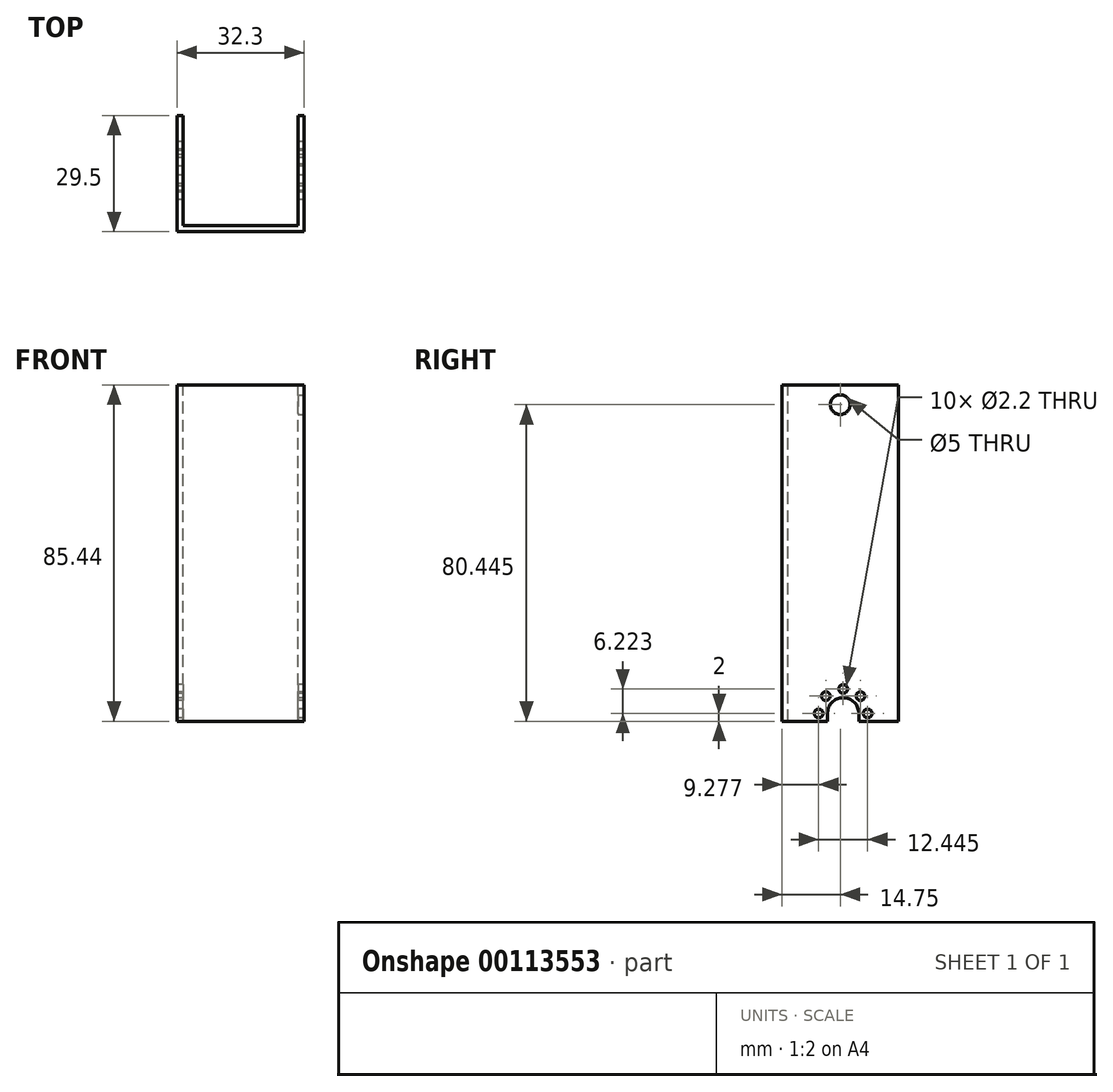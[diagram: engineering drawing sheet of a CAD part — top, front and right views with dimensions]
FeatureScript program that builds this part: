
annotation { "Feature Type Name" : "Feature", "Feature Type Description" : "" }
export const myFeature = defineFeature(function(context is Context, id is Id, definition is map)
    precondition{}
    {
        {
            var Q0;
            Q0=qCreatedBy(makeId("Front.planeOp"),FACE);
            var sketch = newSketch(context, id + "F0", { "sketchPlane" : qUnion([Q0])});
            skLineSegment(sketch, "E0.bottom", {"start": v(0, 0) * mm, "end": v(1.5, 0) * mm});
            skLineSegment(sketch, "E0.top", {"start": v(0, 86.95) * mm, "end": v(32.3, 86.95) * mm});
            skLineSegment(sketch, "E0.left", {"start": v(0, 0) * mm, "end": v(0, 86.95) * mm});
            skLineSegment(sketch, "E0.right", {"start": v(32.3, 0) * mm, "end": v(32.3, 86.95) * mm});
            skLineSegment(sketch, "E1.top", {"start": v(1.5, 85.45) * mm, "end": v(30.8, 85.45) * mm});
            skLineSegment(sketch, "E1.left", {"start": v(1.5, 0) * mm, "end": v(1.5, 85.45) * mm});
            skLineSegment(sketch, "E1.right", {"start": v(30.8, 0) * mm, "end": v(30.8, 85.45) * mm});
            skLineSegment(sketch, "E2.trimOffspring", {"start": v(30.8, 0) * mm, "end": v(32.3, 0) * mm});
            skSolve(sketch);
        }
        {
            var Q0;
            Q0=qSketchRegion(id+"F0",true);
            extrude(context, id + "F1", {"entities" : qUnion([Q0]), "depth" : 28 * mm});
        }
        {
            var Q0;
            Q0=makeQuery(id+"F1.opExtrude","SWEPT_FACE",FACE,{"disambiguationData":[OSD([sQuery(id+"F0.wireOp",EDGE,"E0.left")])]});
            var sketch = newSketch(context, id + "F2", { "sketchPlane" : qUnion([Q0])});
            skArc(sketch, "E3", {"start": v(18, 2) * mm, "mid": v(14, 6) * mm, "end": v(10, 2) * mm});
            skCircle(sketch, "E4", {"center": v(20.22, 2) * mm, "radius": 1.1 * mm});
            skCircle(sketch, "E5.1.0", {"center": v(18.4, 6.4) * mm, "radius": 1.1 * mm});
            skCircle(sketch, "E5.2.0", {"center": v(14, 8.22) * mm, "radius": 1.1 * mm});
            skCircle(sketch, "E5.3.0", {"center": v(9.6, 6.4) * mm, "radius": 1.1 * mm});
            skCircle(sketch, "E5.4.0", {"center": v(7.78, 2) * mm, "radius": 1.1 * mm});
            skLineSegment(sketch, "E6", {"start": v(10, 2) * mm, "end": v(10, 0) * mm});
            skLineSegment(sketch, "E7", {"start": v(18, 2) * mm, "end": v(18, 0) * mm});
            skLineSegment(sketch, "E8", {"start": v(10, 0) * mm, "end": v(18, 0) * mm});
            skLineSegment(sketch, "E9", {"start": v(14, 86.95) * mm, "end": v(14, 0) * mm, "construction": true});
            skPoint(sketch, "E10", {"position": v(14, 0) * mm});
            skLineSegment(sketch, "E11", {"start": v(2.78, 0) * mm, "end": v(0, 0) * mm});
            skLineSegment(sketch, "E12", {"start": v(0, 0) * mm, "end": v(0, 85.45) * mm});
            skLineSegment(sketch, "E13.MirrorCS", {"start": v(28, 0) * mm, "end": v(28, 85.45) * mm});
            skLineSegment(sketch, "E14.MirrorCS", {"start": v(25.22, 0) * mm, "end": v(28, 0) * mm});
            skPoint(sketch, "E15.MirrorCS.end.orphan", {"position": v(28, 85.45) * mm});
            skPoint(sketch, "E15.MirrorCS.start.orphan", {"position": v(25.22, 0) * mm});
            skSolve(sketch);
        }
        {
            var Q0;
            Q0=qSketchRegion(id+"F2",true);
            extrude(context, id + "F3", {"entities" : qUnion([Q0]), "operationType" : NewBodyOperationType.REMOVE, "endBound" : BoundingType.THROUGH_ALL, "oppositeDirection" : true, "depth" : 25 * mm});
        }
        {
            var Q0;
            Q0=makeQuery(id+"F1.opExtrude","SWEPT_FACE",FACE,{"disambiguationData":[OSD([sQuery(id+"F0.wireOp",EDGE,"E0.top")])]});
            var sketch = newSketch(context, id + "F4", { "sketchPlane" : qUnion([Q0])});
            skLineSegment(sketch, "E16", {"start": v(16.15, 0) * mm, "end": v(16.15, -28) * mm, "construction": true});
            skLineSegment(sketch, "E17", {"start": v(0, -14) * mm, "end": v(32.3, -14) * mm, "construction": true});
            skCircle(sketch, "E18", {"center": v(6.15, -4) * mm, "radius": 1.1 * mm});
            skCircle(sketch, "E19.MirrorC", {"center": v(26.15, -4) * mm, "radius": 1.1 * mm});
            skCircle(sketch, "E20.MirrorC", {"center": v(6.15, -24) * mm, "radius": 1.1 * mm});
            skCircle(sketch, "E21.MirrorC", {"center": v(26.15, -24) * mm, "radius": 1.1 * mm});
            skSolve(sketch);
        }
        {
            var Q0;
            Q0=qSketchRegion(id+"F4",true);
            extrude(context, id + "F5", {"entities" : qUnion([Q0]), "operationType" : NewBodyOperationType.REMOVE, "endBound" : BoundingType.UP_TO_NEXT, "oppositeDirection" : true, "depth" : 25 * mm});
        }
        {
            var Q0;
            Q0=makeQuery(id+"F1.opExtrude","SWEPT_FACE",FACE,{"disambiguationData":[OSD([sQuery(id+"F0.wireOp",EDGE,"E0.right")])]});
            var sketch = newSketch(context, id + "F6", { "sketchPlane" : qUnion([Q0])});
            skLineSegment(sketch, "E22.bottom", {"start": v(-28, 86.95) * mm, "end": v(-29.5, 86.95) * mm});
            skLineSegment(sketch, "E22.top", {"start": v(-28, 0) * mm, "end": v(-29.5, 0) * mm});
            skLineSegment(sketch, "E22.left", {"start": v(-28, 86.95) * mm, "end": v(-28, 0) * mm});
            skLineSegment(sketch, "E22.right", {"start": v(-29.5, 86.95) * mm, "end": v(-29.5, 0) * mm});
            skLineSegment(sketch, "E23", {"start": v(-14, 86.95) * mm, "end": v(-14, 0) * mm, "construction": true});
            skLineSegment(sketch, "E24.MirrorCS", {"start": v(0, 86.95) * mm, "end": v(0, 0) * mm});
            skLineSegment(sketch, "E25.MirrorCS", {"start": v(1.5, 86.95) * mm, "end": v(1.5, 0) * mm});
            skLineSegment(sketch, "E26.MirrorCS", {"start": v(0, 86.95) * mm, "end": v(1.5, 86.95) * mm});
            skLineSegment(sketch, "E27.MirrorCS", {"start": v(0, 0) * mm, "end": v(1.5, 0) * mm});
            skSolve(sketch);
        }
        {
            var Q0;
            Q0=makeQuery(id+"F6.imprint","IMPRINT",FACE,{"disambiguationData":[TD([[makeQuery(id+"F6.imprint","IMPRINT",EDGE,{"derivedFrom":sQuery(id+"F6.wireOp",EDGE,"E22.bottom")}),1.0]])]});
            extrude(context, id + "F7", {"entities" : qUnion([Q0]), "operationType" : NewBodyOperationType.ADD, "oppositeDirection" : true, "depth" : 32.3 * mm});
        }
        {
            var Q0;
            Q0=makeQuery(id+"F7.opExtrude","SWEPT_FACE",FACE,{"disambiguationData":[OSD([sQuery(id+"F6.wireOp",EDGE,"E22.right")])]});
            var sketch = newSketch(context, id + "F8", { "sketchPlane" : qUnion([Q0])});
            skPoint(sketch, "E28.centerSnap0", {"position": v(16.15, 0) * mm});
            skLineSegment(sketch, "E29.bottom", {"start": v(0, 86.95) * mm, "end": v(32.3, 86.95) * mm});
            skLineSegment(sketch, "E29.top", {"start": v(0, 85.45) * mm, "end": v(32.3, 85.45) * mm});
            skLineSegment(sketch, "E29.left", {"start": v(0, 86.95) * mm, "end": v(0, 85.45) * mm});
            skLineSegment(sketch, "E29.right", {"start": v(32.3, 86.95) * mm, "end": v(32.3, 85.45) * mm});
            skPoint(sketch, "E29.middle", {"position": v(16.15, 86.2) * mm});
            skLineSegment(sketch, "E30.bottom", {"start": v(1.5, 85.45) * mm, "end": v(30.8, 85.45) * mm});
            skLineSegment(sketch, "E30.top", {"start": v(1.5, 55.45) * mm, "end": v(30.8, 55.45) * mm});
            skLineSegment(sketch, "E30.left", {"start": v(1.5, 85.45) * mm, "end": v(1.5, 55.45) * mm});
            skLineSegment(sketch, "E30.right", {"start": v(30.8, 85.45) * mm, "end": v(30.8, 55.45) * mm});
            skPoint(sketch, "E31", {"position": v(16.15, 85.45) * mm});
            skLineSegment(sketch, "E32.bottom", {"start": v(0, 85.45) * mm, "end": v(1.5, 85.45) * mm});
            skLineSegment(sketch, "E32.top", {"start": v(0, 55.45) * mm, "end": v(1.5, 55.45) * mm});
            skLineSegment(sketch, "E32.left", {"start": v(0, 85.45) * mm, "end": v(0, 55.45) * mm});
            skLineSegment(sketch, "E33.bottom", {"start": v(30.8, 85.45) * mm, "end": v(32.3, 85.45) * mm});
            skLineSegment(sketch, "E33.top", {"start": v(30.8, 55.45) * mm, "end": v(32.3, 55.45) * mm});
            skLineSegment(sketch, "E33.right", {"start": v(32.3, 85.45) * mm, "end": v(32.3, 55.45) * mm});
            skSolve(sketch);
        }
        {
            var Q0;
            Q0=makeQuery(id+"F8.imprint","IMPRINT",FACE,{"disambiguationData":[TD([[makeQuery(id+"F8.imprint","IMPRINT",EDGE,{"derivedFrom":sQuery(id+"F8.wireOp",EDGE,"E30.bottom")}),-1.0]])]});
            var Q1;
            Q1=makeQuery(id+"F8.imprint","IMPRINT",FACE,{"disambiguationData":[TD([[makeQuery(id+"F8.imprint","IMPRINT",EDGE,{"derivedFrom":sQuery(id+"F8.wireOp",EDGE,"E32.bottom")}),-1.0]])]});
            var Q2;
            Q2=makeQuery(id+"F8.imprint","IMPRINT",FACE,{"disambiguationData":[TD([[makeQuery(id+"F8.imprint","IMPRINT",EDGE,{"derivedFrom":sQuery(id+"F8.wireOp",EDGE,"E29.bottom")}),-1.0]])]});
            extrude(context, id + "F9", {"entities" : qUnion([Q0, Q1, Q2]), "operationType" : NewBodyOperationType.REMOVE, "endBound" : BoundingType.THROUGH_ALL, "oppositeDirection" : true, "depth" : 25 * mm});
        }
        {
            var Q0;
            Q0=makeQuery(id+"F7.boolean.opBoolean","MERGE",FACE,{"derivedFrom":[makeQuery(id+"F1.opExtrude","SWEPT_FACE",FACE,{"disambiguationData":[OSD([sQuery(id+"F0.wireOp",EDGE,"E0.right")])]}),makeQuery(id+"F7.opExtrude","CAP_FACE",FACE,{"disambiguationData":[OSD([sQuery(id+"F6.wireOp",EDGE,"E22.bottom"),sQuery(id+"F6.wireOp",EDGE,"E22.top"),sQuery(id+"F6.wireOp",EDGE,"E22.left"),sQuery(id+"F6.wireOp",EDGE,"E22.right")])],"isStart":true})]});
            var sketch = newSketch(context, id + "F10", { "sketchPlane" : qUnion([Q0])});
            skCircle(sketch, "E34", {"center": v(-14.75, 80.45) * mm, "radius": 2.5 * mm});
            skPoint(sketch, "E34.centerSnap0", {"position": v(-14.75, 85.45) * mm});
            skSolve(sketch);
        }
        {
            var Q0;
            Q0=qSketchRegion(id+"F10",true);
            extrude(context, id + "F11", {"entities" : qUnion([Q0]), "operationType" : NewBodyOperationType.REMOVE, "endBound" : BoundingType.UP_TO_NEXT, "oppositeDirection" : true, "depth" : 25 * mm});
        }
    });
